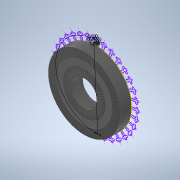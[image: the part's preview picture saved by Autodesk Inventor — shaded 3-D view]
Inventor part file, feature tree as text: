
AUTODESK INVENTOR PART (.ipt)
format: ipt  version: 2022 (Build 260153000, 153)  size: 2,489,344 bytes
history: native  units: in
note: dims shown in document units (in); Inventor stores cm internally (conversion verified against a paired STEP export)
features: other x2, sketch x1
ambient origin geometry x8: Origin, YZ Plane, XZ Plane, XY Plane, X Axis, Y Axis, Z Axis, Center Point
feature tree (3):
  other  "wheel"
  sketch  "Sketch1"  dims[d1=0.5in d2=1.0in d3=0.5in d4=45.0deg d5=1.0in d6=0.5in d7=1.0in d8=1.0in d9=12.5984in d11=360.0deg]
  other  "MeshFeature1"
